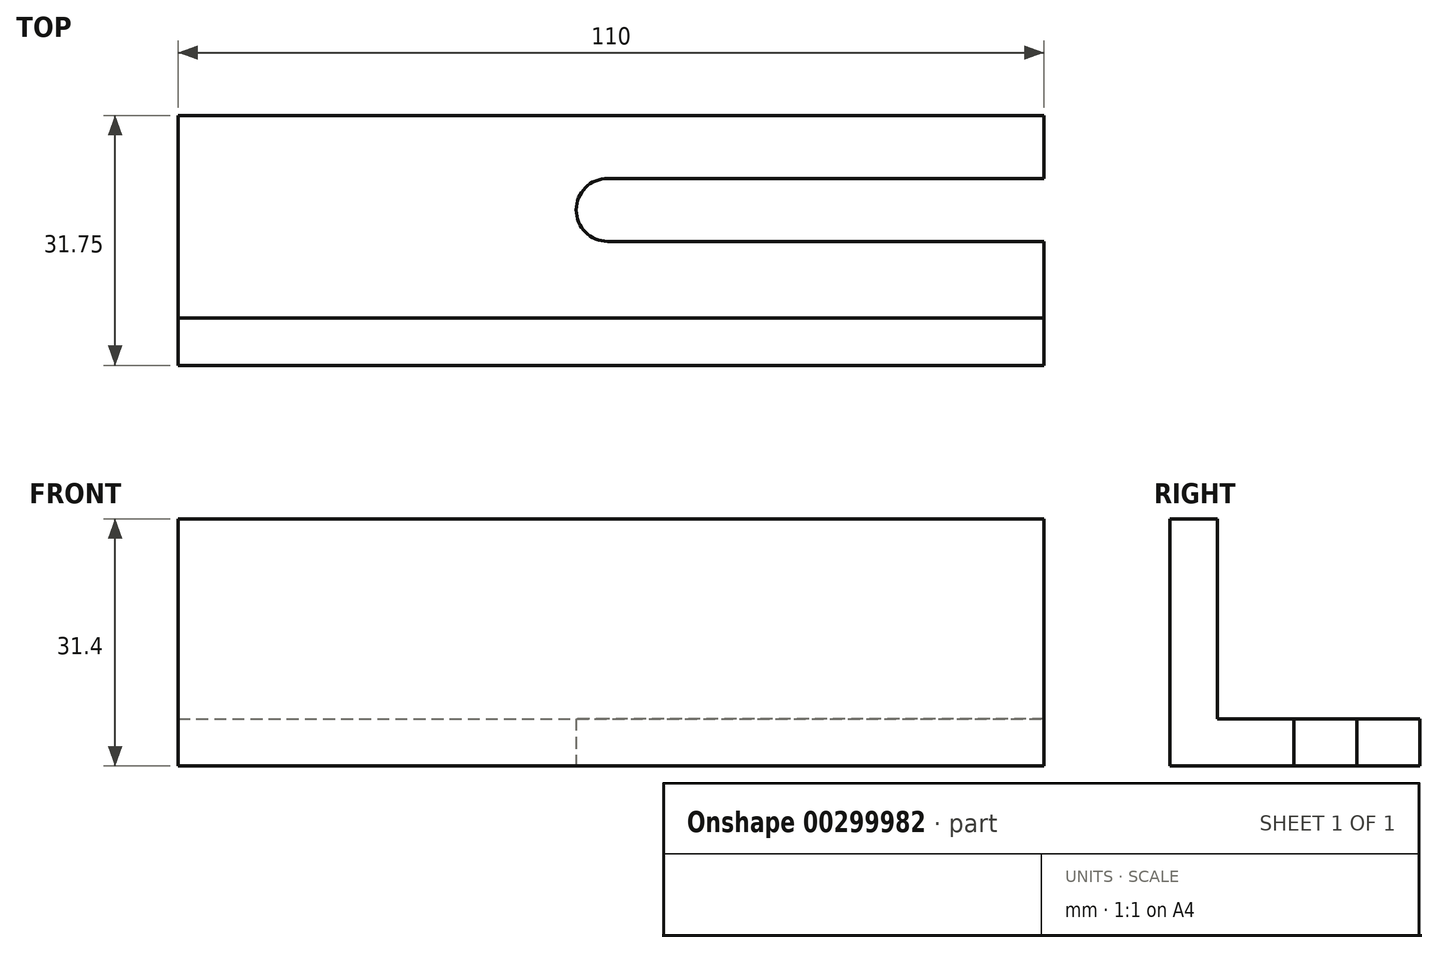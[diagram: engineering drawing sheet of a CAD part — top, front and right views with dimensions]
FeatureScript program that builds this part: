
annotation { "Feature Type Name" : "Feature", "Feature Type Description" : "" }
export const myFeature = defineFeature(function(context is Context, id is Id, definition is map)
    precondition{}
    {
        {
            var Q0;
            Q0=qCreatedBy(makeId("Top.planeOp"),FACE);
            var sketch = newSketch(context, id + "F0", { "sketchPlane" : qUnion([Q0])});
            skLineSegment(sketch, "E0.bottom", {"start": v(0, 0) * mm, "end": v(110, 0) * mm});
            skLineSegment(sketch, "E0.top", {"start": v(0, 31.75) * mm, "end": v(110, 31.75) * mm});
            skLineSegment(sketch, "E0.left", {"start": v(0, 0) * mm, "end": v(0, 31.75) * mm});
            skLineSegment(sketch, "E0.right", {"start": v(110, 0) * mm, "end": v(110, 31.75) * mm});
            skSolve(sketch);
        }
        {
            var Q0;
            Q0 = qSketchRegion(id + "F0", true);
            extrude(context, id + "F1", {"entities" : qUnion([Q0]), "depth" : 6 * mm, "offsetDistance" : 25 * mm});
        }
        {
            var Q0;
            Q0=makeQuery(id+"F1.opExtrude","CAP_FACE",FACE,{"disambiguationData":[OSD([sQuery(id+"F0.wireOp",EDGE,"E0.bottom"),sQuery(id+"F0.wireOp",EDGE,"E0.top"),sQuery(id+"F0.wireOp",EDGE,"E0.left"),sQuery(id+"F0.wireOp",EDGE,"E0.right")])],"isStart":false});
            var sketch = newSketch(context, id + "F2", { "sketchPlane" : qUnion([Q0])});
            skLineSegment(sketch, "E1.bottom", {"start": v(0, 0) * mm, "end": v(110, 0) * mm});
            skLineSegment(sketch, "E1.top", {"start": v(0, 6) * mm, "end": v(110, 6) * mm});
            skLineSegment(sketch, "E1.left", {"start": v(0, 0) * mm, "end": v(0, 6) * mm});
            skLineSegment(sketch, "E1.right", {"start": v(110, 0) * mm, "end": v(110, 6) * mm});
            skSolve(sketch);
        }
        {
            var Q0;
            Q0 = qSketchRegion(id + "F2", true);
            extrude(context, id + "F3", {"entities" : qUnion([Q0]), "operationType" : NewBodyOperationType.ADD, "depth" : 25.4 * mm, "offsetDistance" : 25 * mm});
        }
        {
            var Q0;
            Q0=makeQuery(id+"F1.opExtrude","CAP_FACE",FACE,{"disambiguationData":[OSD([sQuery(id+"F0.wireOp",EDGE,"E0.bottom"),sQuery(id+"F0.wireOp",EDGE,"E0.top"),sQuery(id+"F0.wireOp",EDGE,"E0.left"),sQuery(id+"F0.wireOp",EDGE,"E0.right")])],"isStart":true});
            var sketch = newSketch(context, id + "F4", { "sketchPlane" : qUnion([Q0])});
            skCircle(sketch, "E2", {"center": v(54.56, -19.75) * mm, "radius": 4 * mm});
            skLineSegment(sketch, "E3", {"start": v(54.56, -19.75) * mm, "end": v(54.56, -15.75) * mm});
            skLineSegment(sketch, "E4", {"start": v(54.56, -15.75) * mm, "end": v(110, -15.75) * mm});
            skLineSegment(sketch, "E5", {"start": v(54.56, -19.75) * mm, "end": v(54.56, -23.75) * mm});
            skLineSegment(sketch, "E6", {"start": v(54.56, -23.75) * mm, "end": v(110, -23.75) * mm});
            skLineSegment(sketch, "E7", {"start": v(110, -23.75) * mm, "end": v(110, -15.75) * mm});
            skSolve(sketch);
        }
        {
            var Q0;
            Q0 = qSketchRegion(id + "F4", true);
            extrude(context, id + "F5", {"entities" : qUnion([Q0]), "operationType" : NewBodyOperationType.REMOVE, "endBound" : BoundingType.THROUGH_ALL, "oppositeDirection" : true, "depth" : 25 * mm, "offsetDistance" : 25 * mm});
        }
    });
